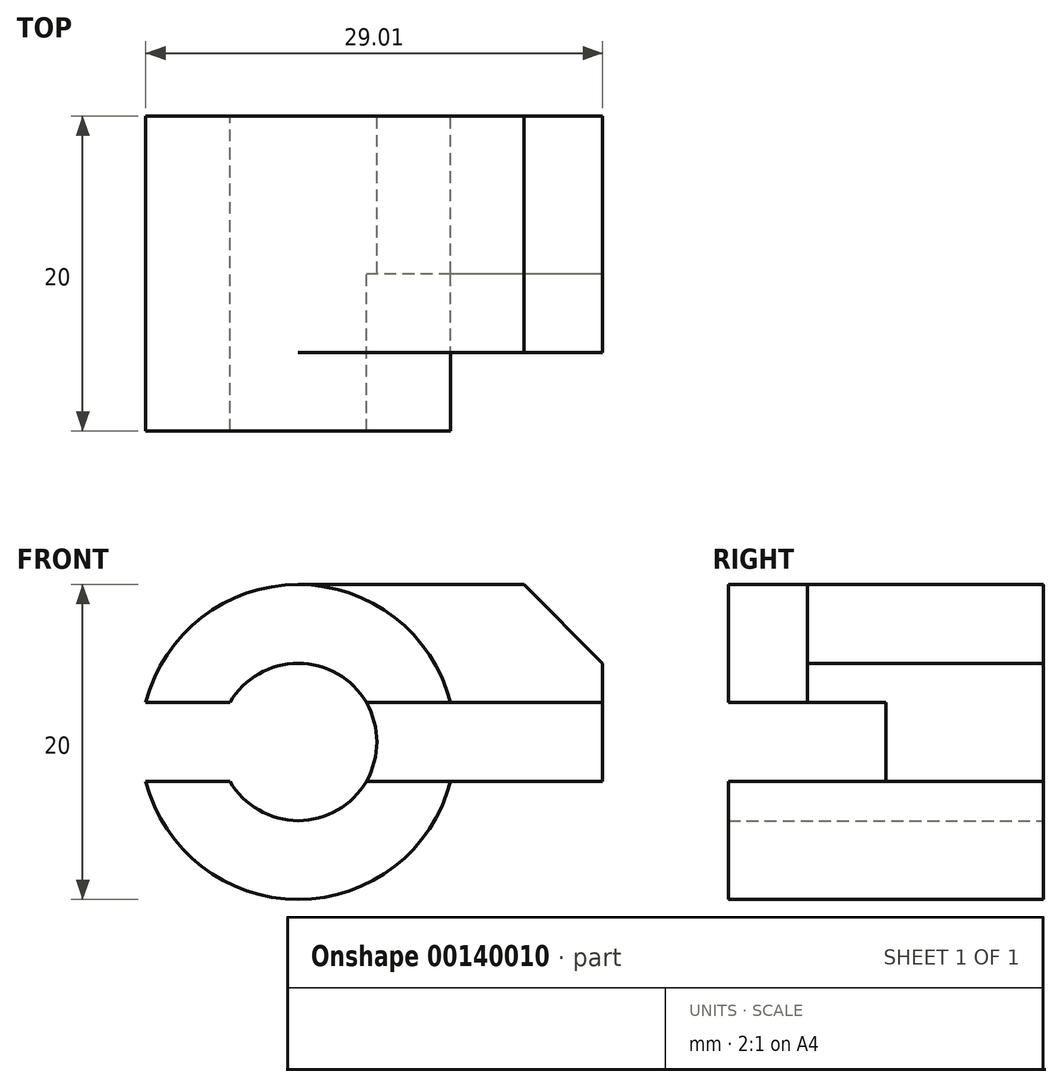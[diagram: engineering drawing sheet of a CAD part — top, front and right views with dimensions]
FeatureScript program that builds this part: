
annotation { "Feature Type Name" : "Feature", "Feature Type Description" : "" }
export const myFeature = defineFeature(function(context is Context, id is Id, definition is map)
    precondition{}
    {
        {
            var Q0;
            Q0=qCreatedBy(makeId("Front.planeOp"),FACE);
            var sketch = newSketch(context, id + "F0", { "sketchPlane" : qUnion([Q0])});
            skLineSegment(sketch, "E0", {"start": v(-18.2, 0) * mm, "end": v(24.23, 0) * mm, "construction": true});
            skArc(sketch, "E1", {"start": v(5, 0) * mm, "mid": v(0, 5) * mm, "end": v(-5, 0) * mm});
            skLineSegment(sketch, "E2", {"start": v(-4.33, 2.5) * mm, "end": v(-9.68, 2.5) * mm});
            skLineSegment(sketch, "E3", {"start": v(4.33, 2.5) * mm, "end": v(19.33, 2.5) * mm});
            skLineSegment(sketch, "E4", {"start": v(19.33, 0) * mm, "end": v(19.33, 2.5) * mm});
            skLineSegment(sketch, "E5", {"start": v(19.33, 2.5) * mm, "end": v(19.33, 5) * mm});
            skLineSegment(sketch, "E6", {"start": v(19.33, 5) * mm, "end": v(14.33, 10) * mm});
            skLineSegment(sketch, "E7", {"start": v(14.33, 10) * mm, "end": v(0, 10) * mm});
            skArc(sketch, "E8", {"start": v(0, 10) * mm, "mid": v(-7.07, 7.07) * mm, "end": v(-10, 0) * mm});
            skArc(sketch, "E9", {"start": v(9.68, 2.5) * mm, "mid": v(6.12, 7.9) * mm, "end": v(0, 10) * mm});
            skLineSegment(sketch, "E10", {"start": v(9.68, 2.5) * mm, "end": v(4.33, 2.5) * mm});
            skArc(sketch, "E11.MirrorCS", {"start": v(0, -10) * mm, "mid": v(-7.07, -7.07) * mm, "end": v(-10, 0) * mm});
            skLineSegment(sketch, "E12.MirrorCS", {"start": v(-4.33, -2.5) * mm, "end": v(-9.68, -2.5) * mm});
            skArc(sketch, "E13.MirrorCS", {"start": v(5, 0) * mm, "mid": v(0, -5) * mm, "end": v(-5, 0) * mm});
            skArc(sketch, "E14.MirrorCS", {"start": v(9.68, -2.5) * mm, "mid": v(6.12, -7.9) * mm, "end": v(0, -10) * mm});
            skLineSegment(sketch, "E15.MirrorCS", {"start": v(9.68, -2.5) * mm, "end": v(4.33, -2.5) * mm});
            skLineSegment(sketch, "E16.MirrorCS", {"start": v(4.33, -2.5) * mm, "end": v(19.33, -2.5) * mm});
            skLineSegment(sketch, "E17.MirrorCS", {"start": v(19.33, 0) * mm, "end": v(19.33, -2.5) * mm});
            skLineSegment(sketch, "E18.MirrorCS", {"start": v(19.33, -2.5) * mm, "end": v(19.33, -5) * mm});
            skLineSegment(sketch, "E19.MirrorCS", {"start": v(19.33, -5) * mm, "end": v(14.33, -10) * mm});
            skLineSegment(sketch, "E20.MirrorCS", {"start": v(14.33, -10) * mm, "end": v(0, -10) * mm});
            skArc(sketch, "E21", {"start": v(9.68, 2.5) * mm, "mid": v(10, 0) * mm, "end": v(9.68, -2.5) * mm});
            skArc(sketch, "E22", {"start": v(-9.68, 2.5) * mm, "mid": v(-10, 0) * mm, "end": v(-9.68, -2.5) * mm});
            skSolve(sketch);
        }
        {
            var Q0;
            {var subQ2=sQuery(id+"F0.wireOp",EDGE,"E2");Q0=makeQuery(id+"F0.imprint","IMPRINT",FACE,{"disambiguationData":[TD([[makeQuery(id+"F0.imprint","IMPRINT",EDGE,{"derivedFrom":subQ2}),-1.0]])]});}
            var Q1;
            {var subQ2=sQuery(id+"F0.wireOp",EDGE,"E12.MirrorCS");Q1=makeQuery(id+"F0.imprint","IMPRINT",FACE,{"disambiguationData":[TD([[makeQuery(id+"F0.imprint","IMPRINT",EDGE,{"derivedFrom":subQ2}),1.0]])]});}
            var Q2;
            {var subQ7=sQuery(id+"F0.wireOp",EDGE,"E2");Q2=makeQuery(id+"F0.imprint","IMPRINT",FACE,{"disambiguationData":[TD([[makeQuery(id+"F0.imprint","IMPRINT",EDGE,{"derivedFrom":subQ7}),1.0]])]});}
            extrude(context, id + "F1", {"entities" : qUnion([Q0, Q1, Q2]), "depth" : 20 * mm});
        }
        {
            var Q0;
            Q0=makeQuery(id+"F0.imprint","IMPRINT",FACE,{"disambiguationData":[TD([[makeQuery(id+"F0.imprint","IMPRINT",EDGE,{"derivedFrom":sQuery(id+"F0.wireOp",EDGE,"E3")}),1.0]])]});
            var Q1;
            {var subQ2=sQuery(id+"F0.wireOp",EDGE,"E14.MirrorCS");Q1=makeQuery(id+"F0.imprint","IMPRINT",FACE,{"disambiguationData":[TD([[makeQuery(id+"F0.imprint","IMPRINT",EDGE,{"derivedFrom":subQ2}),1.0]])]});}
            extrude(context, id + "F2", {"entities" : qUnion([Q0, Q1]), "operationType" : NewBodyOperationType.ADD, "depth" : 15 * mm});
        }
        {
            var Q0;
            Q0=makeQuery(id+"F0.imprint","IMPRINT",FACE,{"disambiguationData":[TD([[makeQuery(id+"F0.imprint","IMPRINT",EDGE,{"derivedFrom":sQuery(id+"F0.wireOp",EDGE,"E3")}),-1.0]])]});
            extrude(context, id + "F3", {"entities" : qUnion([Q0]), "operationType" : NewBodyOperationType.ADD, "depth" : 10 * mm});
        }
        {
            var Q0;
            {var subQ4=sQuery(id+"F0.wireOp",EDGE,"E2");Q0=makeQuery(id+"F0.imprint","IMPRINT",FACE,{"disambiguationData":[TD([[makeQuery(id+"F0.imprint","IMPRINT",EDGE,{"derivedFrom":subQ4}),1.0]])]});}
            extrude(context, id + "F4", {"entities" : qUnion([Q0]), "operationType" : NewBodyOperationType.REMOVE, "depth" : 25 * mm});
        }
    });
